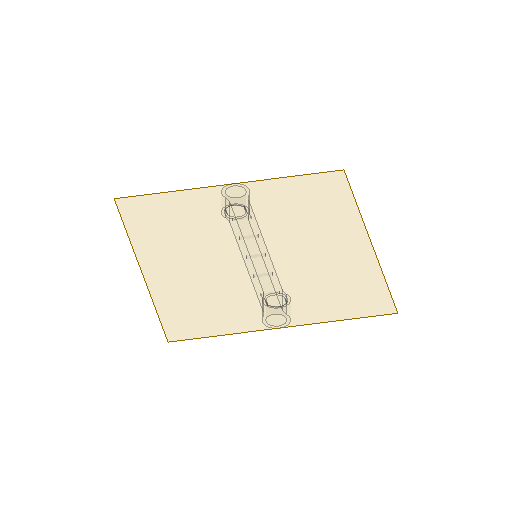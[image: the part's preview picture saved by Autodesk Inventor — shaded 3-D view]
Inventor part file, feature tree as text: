
AUTODESK INVENTOR PART (.ipt)
format: ipt  version: 2024.2 (Build 282272000, 272)  size: 141,312 bytes
history: native  units: in
note: dims shown in document units (in); Inventor stores cm internally (conversion verified against a paired STEP export)
features: other x4, plane x1
ambient origin geometry x8: Origin, YZ Plane, XZ Plane, XY Plane, X Axis, Y Axis, Z Axis, Center Point
bodies: Body1 (feature_tree)
feature tree (5):
  other  "5 Barras Version 0.ipt"
  plane  "Work Plane1"
  other  "Distal Link 1::5 Barras Version 0.ipt"
  other  "TaggingFeature1"
  other  "Distal Link 1"
